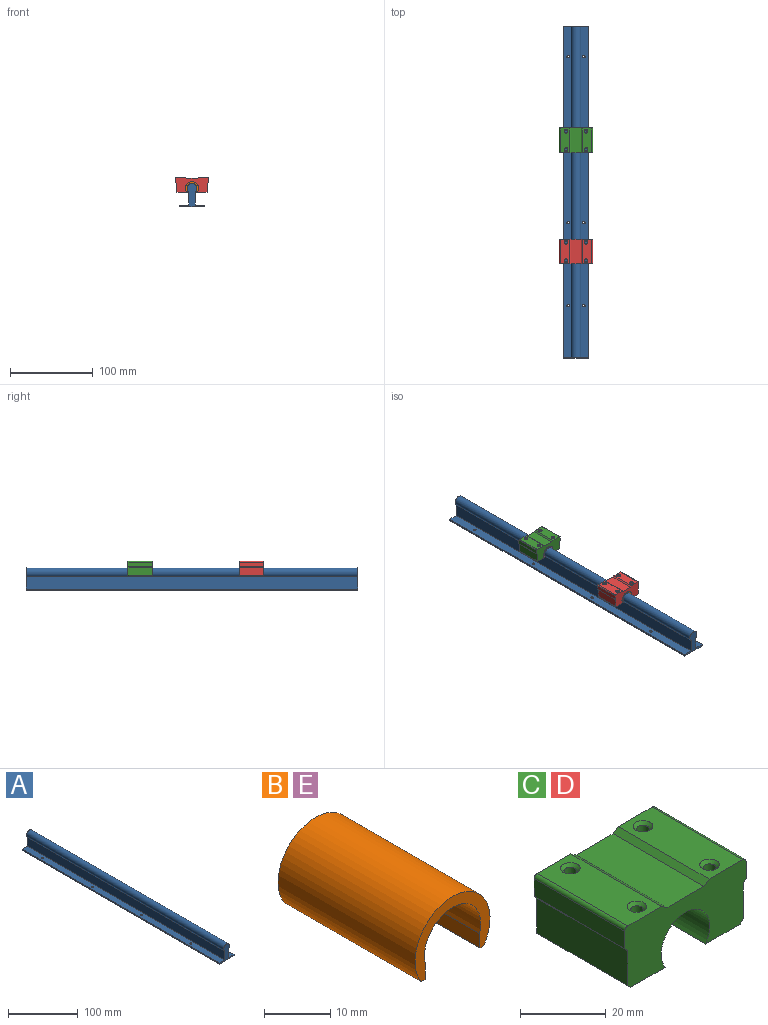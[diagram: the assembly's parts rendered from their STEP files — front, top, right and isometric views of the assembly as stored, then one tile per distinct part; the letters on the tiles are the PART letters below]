
ASSEMBLY  parts=5 mates=4
PART A: 18 faces, bbox 30x400x28 mm
  f0: cylinder r=1.5mm len=3mm, axis (0,0,1), area 18.8mm2, adj f6,f12
  f1: cylinder r=1.5mm len=3mm, axis (0,0,1), area 18.8mm2, adj f6,f12
  f2: cylinder r=1.5mm len=3mm, axis (0,0,1), area 18.8mm2, adj f6,f12
  f3: cylinder r=1.5mm len=3mm, axis (0,0,1), area 18.8mm2, adj f6,f8
  f4: cylinder r=1.5mm len=3mm, axis (0,0,1), area 18.8mm2, adj f6,f8
  f5: cylinder r=1.5mm len=3mm, axis (0,0,1), area 18.8mm2, adj f6,f8
  f6: plane 400x30mm, normal (0,0,-1), area 11943.5mm2, adj f0,f1,f2,f3,f4,f5,f7,f13
  f7: plane 400x2mm, normal (1,0,0), area 800mm2, adj f6,f8,f14,f15
  f8: plane 400x11mm, normal (0,0,1), area 4371.7mm2, adj f3,f4,f5,f7,f9,f14,f15,f16
  f9: plane 400x15.53mm, normal (1,0,0), area 6211.1mm2, adj f8,f10,f14,f15
  f10: cylinder r=6mm len=400mm, axis (0,1,0), area 11577mm2, adj f9,f11,f14,f15
  f11: plane 400x15.53mm, normal (-1,0,0), area 6211.1mm2, adj f10,f12,f14,f15
  f12: plane 400x11mm, normal (0,0,1), area 4371.7mm2, adj f0,f1,f2,f11,f13,f14,f15,f17
  f13: plane 400x2mm, normal (-1,0,0), area 800mm2, adj f6,f12,f14,f15
  f14: plane 30x28mm, normal (0,-1,0), area 288.9mm2, adj f6,f7,f8,f9,f10,f11,f12,f13
  f15: plane 30x28mm, normal (0,1,0), area 288.9mm2, adj f6,f7,f8,f9,f10,f11,f12,f13
  f16: cylinder r=1.5mm len=3mm, axis (0,0,1), area 18.8mm2, adj f6,f8
  f17: cylinder r=1.5mm len=3mm, axis (0,0,1), area 18.8mm2, adj f6,f12
PART B: 8 faces, bbox 16x29.3x12.4 mm
  f0: cylinder r=6mm len=29.28mm, axis (0,1,0), area 655mm2, adj f2,f3,f6,f7
  f1: cylinder r=8mm len=29.28mm, axis (0,1,0), area 1009.3mm2, adj f2,f3,f4,f5
  f2: plane 16x12.41mm, normal (0,-1,0), area 59.3mm2, adj f0,f1,f4,f5,f6,f7
  f3: plane 16x12.41mm, normal (0,1,0), area 59.3mm2, adj f0,f1,f4,f5,f6,f7
  f4: plane 29.28x0.85mm, normal (0,0,-1), area 24.8mm2, adj f1,f2,f3,f6
  f5: plane 29.28x0.85mm, normal (0,0,-1), area 24.8mm2, adj f1,f2,f3,f7
  f6: plane 29.28x2.67mm, normal (-1,0,-0.03), area 78.3mm2, adj f0,f2,f3,f4
  f7: plane 29.28x2.67mm, normal (1,0,-0.03), area 78.3mm2, adj f0,f2,f3,f5
PART C: 28 faces, bbox 40x30x18 mm
  f0: plane 30x11.43mm, normal (0,0,-1), area 328.9mm2, adj f1,f2,f3,f4,f23,f25
  f1: plane 40x18mm, normal (0,-1,0), area 514.1mm2, adj f0,f7,f8,f9,f10,f11,f12,f13
  f2: plane 40x18mm, normal (0,1,0), area 514.1mm2, adj f0,f7,f8,f9,f10,f11,f12,f13
  f3: cylinder r=1.5mm len=17.2mm, axis (0,0,1), area 162.1mm2, adj f0,f20
  f4: cylinder r=1.5mm len=17.2mm, axis (0,0,1), area 162.1mm2, adj f0,f19
  f5: cylinder r=1.5mm len=17.2mm, axis (0,0,1), area 162.1mm2, adj f15,f21
  f6: cylinder r=1.5mm len=17.2mm, axis (0,0,1), area 162.1mm2, adj f15,f22
  f7: plane 30x11.19mm, normal (0,0,1), area 302.3mm2, adj f1,f2,f8,f19,f20,f27
  f8: plane 30x1.71mm, normal (-0.57,0,0.82), area 62.8mm2, adj f1,f2,f7,f9
  f9: plane 30x12.2mm, normal (0,0,1), area 366mm2, adj f1,f2,f8,f10
  f10: plane 30x1.71mm, normal (0.57,0,0.82), area 62.8mm2, adj f1,f2,f9,f11
  f11: plane 30x11.19mm, normal (0,0,1), area 302.3mm2, adj f1,f2,f10,f21,f22,f26
  f12: plane 30x5mm, normal (-1,0,0), area 150mm2, adj f1,f2,f13,f26
  f13: plane 30x1mm, normal (-0.75,0,-0.66), area 40.2mm2, adj f1,f2,f12,f14
  f14: plane 30x10mm, normal (-1,0,0), area 300mm2, adj f1,f2,f13,f24
  f15: plane 30x11.43mm, normal (0,0,-1), area 328.9mm2, adj f1,f2,f5,f6,f23,f24
  f16: plane 30x10mm, normal (1,0,0), area 300mm2, adj f1,f2,f17,f25
  f17: plane 30x1mm, normal (0.75,0,-0.66), area 40.2mm2, adj f1,f2,f16,f18
  f18: plane 30x5mm, normal (1,0,0), area 150mm2, adj f1,f2,f17,f27
  f19: cone r=1.5mm half-angle=45deg, axis (0,0,1), area 13.5mm2, adj f4,f7
  f20: cone r=1.5mm half-angle=45deg, axis (0,0,1), area 13.5mm2, adj f3,f7
  f21: cone r=1.5mm half-angle=45deg, axis (0,0,1), area 13.5mm2, adj f5,f11
  f22: cone r=1.5mm half-angle=45deg, axis (0,0,1), area 13.5mm2, adj f6,f11
  f23: cylinder r=8mm len=30mm, axis (0,-1,0), area 1034.1mm2, adj f0,f1,f2,f15
  f24: plane 30x1mm, normal (-0.71,0,-0.71), area 42.4mm2, adj f1,f2,f14,f15
  f25: plane 30x1mm, normal (0.71,0,-0.71), area 42.4mm2, adj f0,f1,f2,f16
  f26: cylinder r=1mm len=30mm, axis (0,-1,0), area 47.1mm2, adj f1,f2,f11,f12
  f27: cylinder r=1mm len=30mm, axis (0,1,0), area 47.1mm2, adj f1,f2,f7,f18
PART D: same geometry as C
PART E: same geometry as B
PLACE A t=(-48.94,0,43.04)mm fixed
PLACE B t=(-48.94,-71.73,43.04)mm
PLACE C t=(-48.94,62.13,43.04)mm
PLACE D t=(-48.94,-71.73,43.04)mm
PLACE E t=(-48.94,62.13,43.04)mm
MATE fastened B.f0 <-> D.f23  axis (0,1,0) through (-48.94,-71.73,29.45)mm
MATE slider B.f0 <-> A.f10  axis (0,1,0) through (-48.94,-71.73,29.45)mm
MATE fastened E.f0 <-> C.f23  axis (0,1,0) through (-48.94,62.13,29.45)mm
MATE slider E.f0 <-> A.f10  axis (0,1,0) through (-48.94,62.13,29.45)mm
